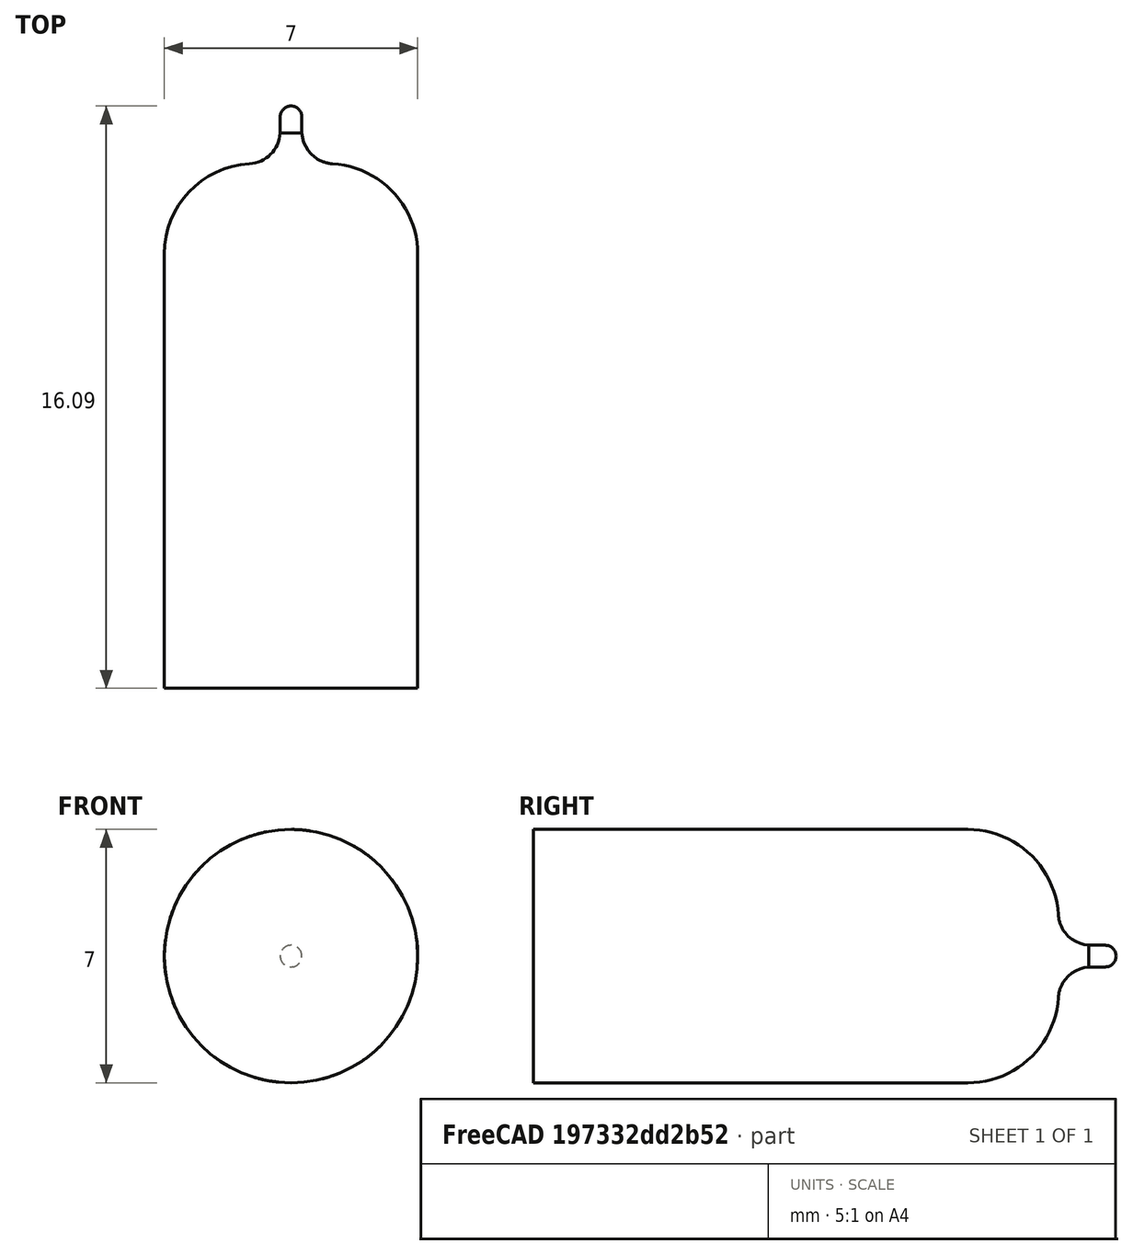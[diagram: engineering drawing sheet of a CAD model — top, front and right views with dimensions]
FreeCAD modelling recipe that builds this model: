
FCSTD DOCUMENT  (FreeCAD 0.16R6712 (Git))
Label: bulb
License: All rights reserved
LicenseURL: http://en.wikipedia.org/wiki/All_rights_reserved
objects: Sketcher::SketchObject×1, PartDesign::Revolution×1, Mesh::Feature×1
note: 3 computed .brp shape members not serialized (recipe doc carries the construction recipe); baked Part::Feature solids carry a one-line shape summary decoded from their .brp

FEATURE [Sketcher::SketchObject] Sketch
  sketch-geometry (7):
    g0: LineSegment StartX=-3.5 StartY=10 StartZ=0 EndX=-3.5 EndY=-2 EndZ=0
    g1: ArcOfCircle CenterX=-1 CenterY=10 CenterZ=0 NormalX=0 NormalY=0 NormalZ=1 Radius=2.5 StartAngle=1.63077 EndAngle=3.14159
    g2: LineSegment StartX=-3.5 StartY=-2 StartZ=0 EndX=0 EndY=-2 EndZ=0
    g3: ArcOfCircle CenterX=-1.20413 CenterY=13.3998 CenterZ=0 NormalX=0 NormalY=0 NormalZ=1 Radius=0.905908 StartAngle=4.77235 EndAngle=6.22052
    g4: LineSegment StartX=0 StartY=14.0931 StartZ=0 EndX=0 EndY=-2 EndZ=0
    g5: LineSegment StartX=-0.3 StartY=13.3431 StartZ=0 EndX=-0.3 EndY=13.7931 EndZ=0
    g6: ArcOfCircle CenterX=0 CenterY=13.7931 CenterZ=0 NormalX=0 NormalY=0 NormalZ=1 Radius=0.3 StartAngle=1.5708 EndAngle=3.14159
  constraints (23):
    c: Vertical(g0)
    c: DistanceX(g-2,g0) = -3.5
    c: Coincident(g1,g0)
    c: Tangent(g1,g0)
    c: Radius(g1) = 2.5
    c: Horizontal(g2)
    c: PointOnObject(g2,g-2)
    c: Coincident(g3,g1)
    c: Tangent(g1,g3)
    c: DistanceY(g-1,g2) = -2
    c: Coincident(g4,g2)
    c: Coincident(g5,g3)
    c: Vertical(g5)
    c: PointOnObject(g6,g4)
    c: Coincident(g6,g5)
    c: PointOnObject(g6,g4)
    c: Tangent(g5,g6)
    c: Radius(g6) = 0.3
    c: Coincident(g4,g6)
    c: PointOnObject(g4,g-2)
    c: Distance(g0,g2) = 12
    c: DistanceY(g3,g4) = 0.75
    c: Coincident(g2,g0)
FEATURE [PartDesign::Revolution] Revolution
  Angle = 360
  Axis = (0,1,0)
  Base = (0,0,0)
  ReferenceAxis = -> Sketch [V_Axis]
  Sketch = -> Sketch
FEATURE [Mesh::Feature] Mesh  label="Revolution (Meshed)"
